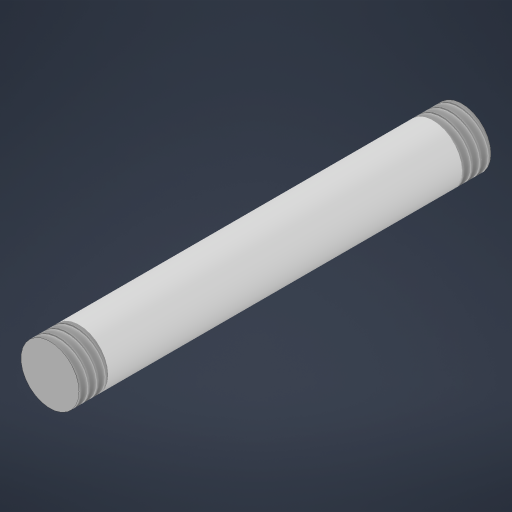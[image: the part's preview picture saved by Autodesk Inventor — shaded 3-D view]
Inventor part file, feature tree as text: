
AUTODESK INVENTOR PART (.ipt)
format: ipt  version: 2023 (Build 270158000, 158)  size: 181,760 bytes
history: native  units: mm
features: thread x2, extrude x1, sketch x1
ambient origin geometry x8: Origin, YZ Plane, XZ Plane, XY Plane, X Axis, Y Axis, Z Axis, Center Point
bodies: Solid1 (feature_tree)
feature tree (4):
  extrude  "Extrusion1"  Depth=71.0mm TaperAngle=0.0deg
  thread  "Thread1"  [1 undecoded]
  thread  "Thread2"  [1 undecoded]
  sketch  "Sketch1"  dims[d0=10.0mm d1=71.0mm d2=0.0mm d3=5.0mm d4=0.0mm d5=5.0mm d6=0.0mm]
note: 2 required parameter values undecoded (feature->parameter linkage not recoverable at this tier; creation-order binding heuristic only, values carry confidence <= 0.55)
